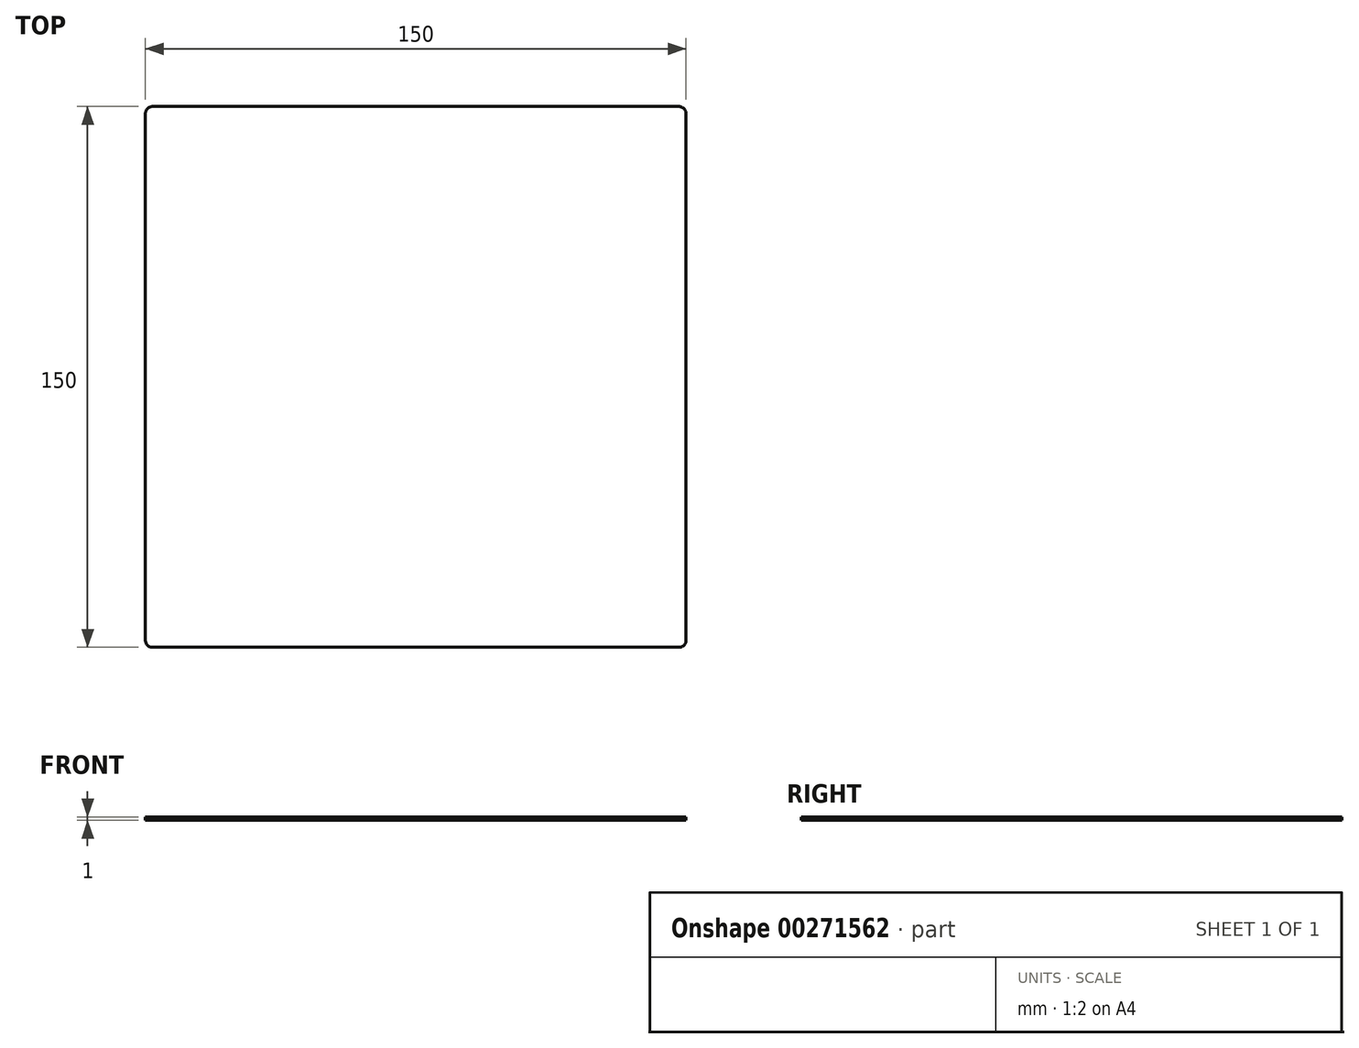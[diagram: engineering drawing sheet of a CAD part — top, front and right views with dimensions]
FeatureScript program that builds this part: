
annotation { "Feature Type Name" : "Feature", "Feature Type Description" : "" }
export const myFeature = defineFeature(function(context is Context, id is Id, definition is map)
    precondition{}
    {
        {
            var Q0;
            Q0=qCreatedBy(makeId("Top.planeOp"),FACE);
            var sketch = newSketch(context, id + "F0", { "sketchPlane" : qUnion([Q0])});
            skLineSegment(sketch, "E0.bottom", {"start": v(0, 0) * mm, "end": v(150, 0) * mm});
            skLineSegment(sketch, "E0.top", {"start": v(0, -150) * mm, "end": v(150, -150) * mm});
            skLineSegment(sketch, "E0.left", {"start": v(0, 0) * mm, "end": v(0, -150) * mm});
            skLineSegment(sketch, "E0.right", {"start": v(150, 0) * mm, "end": v(150, -150) * mm});
            skSolve(sketch);
        }
        {
            var Q0;
            Q0 = qSketchRegion(id + "F0", true);
            var Q1;
            Q1=sQuery(id+"F0.wireOp",EDGE,"E0.left");
            var Q2;
            Q2=sQuery(id+"F0.wireOp",EDGE,"E0.bottom");
            extrude(context, id + "F1", {"entities" : qUnion([Q0]), "surfaceEntities" : qUnion([Q1, Q2]), "depth" : 1 * mm});
        }
        {
            var Q0;
            Q0=makeQuery(id+"F1.opExtrude","SWEPT_EDGE",EDGE,{"disambiguationData":[OSD([sQuery(id+"F0.wireOp",EDGE,"E0.top"),sQuery(id+"F0.wireOp",EDGE,"E0.left")])]});
            var Q1;
            Q1=makeQuery(id+"F1.opExtrude","SWEPT_EDGE",EDGE,{"disambiguationData":[OSD([sQuery(id+"F0.wireOp",EDGE,"E0.bottom"),sQuery(id+"F0.wireOp",EDGE,"E0.left")])]});
            var Q2;
            Q2=makeQuery(id+"F1.opExtrude","SWEPT_EDGE",EDGE,{"disambiguationData":[OSD([sQuery(id+"F0.wireOp",EDGE,"E0.top"),sQuery(id+"F0.wireOp",EDGE,"E0.right")])]});
            var Q3;
            Q3=makeQuery(id+"F1.opExtrude","SWEPT_EDGE",EDGE,{"disambiguationData":[OSD([sQuery(id+"F0.wireOp",EDGE,"E0.bottom"),sQuery(id+"F0.wireOp",EDGE,"E0.right")])]});
            fillet(context, id + "F2", {"entities" : qUnion([Q0, Q1, Q2, Q3]), "radius" : 2 * mm, "tangentPropagation" : true, "allowEdgeOverflow" : false});
        }
    });
